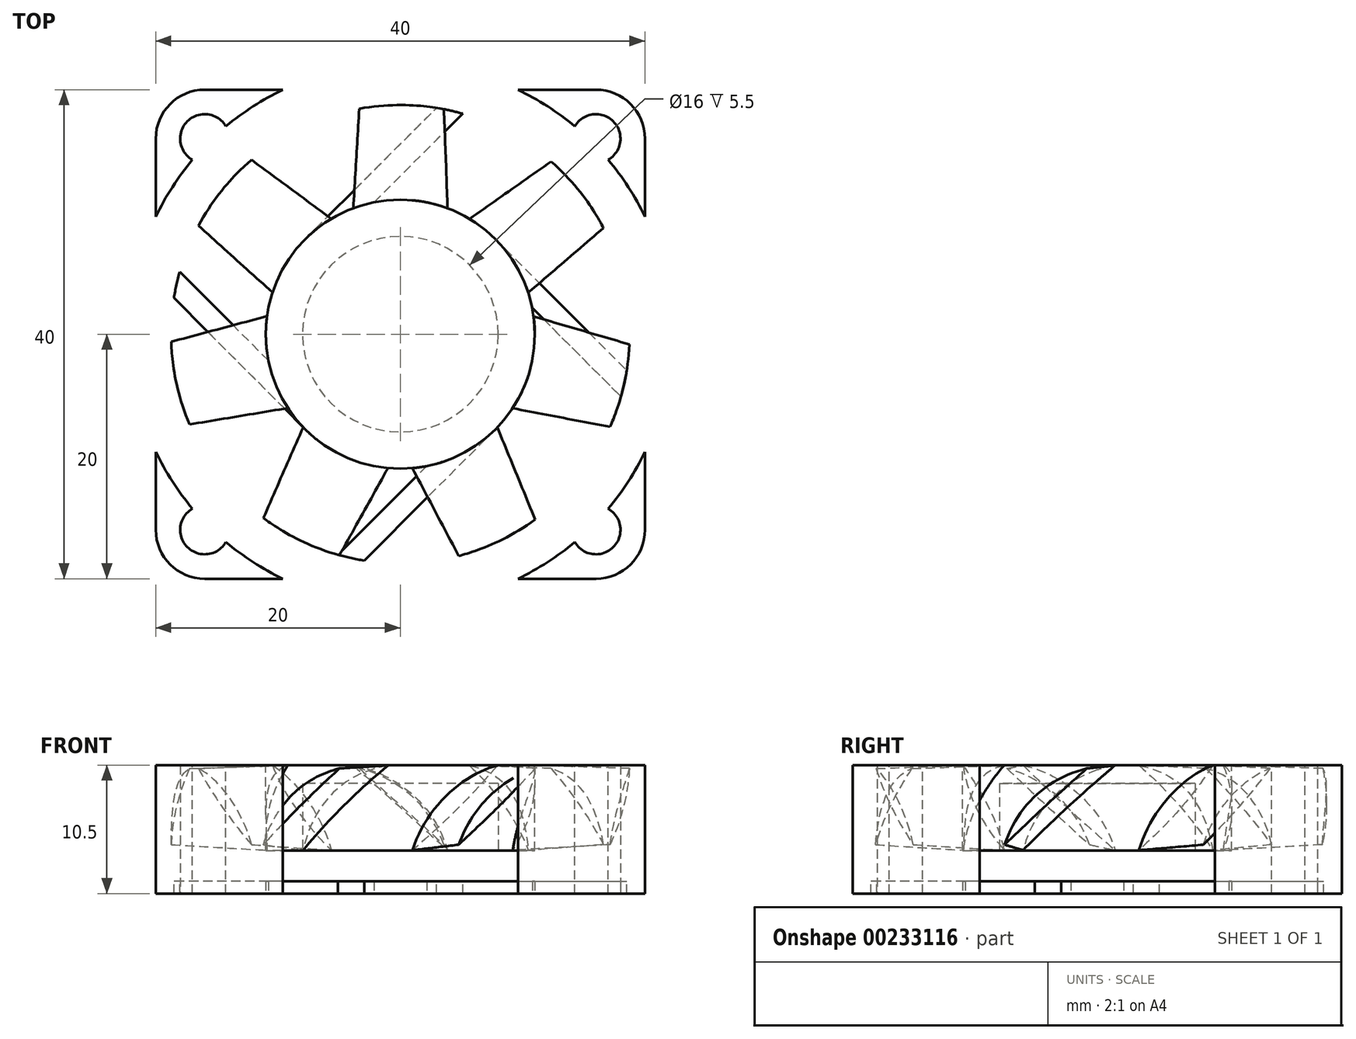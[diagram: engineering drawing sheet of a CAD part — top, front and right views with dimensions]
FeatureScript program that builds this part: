
annotation { "Feature Type Name" : "Feature", "Feature Type Description" : "" }
export const myFeature = defineFeature(function(context is Context, id is Id, definition is map)
    precondition{}
    {
        {
            var Q0;
            Q0=qCreatedBy(makeId("Top.planeOp"),FACE);
            var sketch = newSketch(context, id + "F0", { "sketchPlane" : qUnion([Q0])});
            skLineSegment(sketch, "E0.bottom", {"start": v(16, 20) * mm, "end": v(-16, 20) * mm});
            skLineSegment(sketch, "E0.top", {"start": v(16, -20) * mm, "end": v(-16, -20) * mm});
            skLineSegment(sketch, "E0.left", {"start": v(20, 16) * mm, "end": v(20, -16) * mm});
            skLineSegment(sketch, "E0.right", {"start": v(-20, 16) * mm, "end": v(-20, -16) * mm});
            skPoint(sketch, "E0.middle", {"position": v(0, 0) * mm});
            skPoint(sketch, "E1.visualSharp", {"position": v(20, 20) * mm});
            skArc(sketch, "E1.filletArc", {"start": v(20, 16) * mm, "mid": v(18.83, 18.83) * mm, "end": v(16, 20) * mm});
            skPoint(sketch, "E2.visualSharp", {"position": v(-20, 20) * mm});
            skArc(sketch, "E2.filletArc", {"start": v(-16, 20) * mm, "mid": v(-18.83, 18.83) * mm, "end": v(-20, 16) * mm});
            skPoint(sketch, "E3.visualSharp", {"position": v(-20, -20) * mm});
            skArc(sketch, "E3.filletArc", {"start": v(-20, -16) * mm, "mid": v(-18.83, -18.83) * mm, "end": v(-16, -20) * mm});
            skPoint(sketch, "E4.visualSharp", {"position": v(20, -20) * mm});
            skArc(sketch, "E4.filletArc", {"start": v(16, -20) * mm, "mid": v(18.83, -18.83) * mm, "end": v(20, -16) * mm});
            skLineSegment(sketch, "E5.bottom", {"start": v(-16, 16) * mm, "end": v(16, 16) * mm, "construction": true});
            skLineSegment(sketch, "E5.top", {"start": v(-16, -16) * mm, "end": v(16, -16) * mm, "construction": true});
            skLineSegment(sketch, "E5.left", {"start": v(-16, 16) * mm, "end": v(-16, -16) * mm, "construction": true});
            skLineSegment(sketch, "E5.right", {"start": v(16, 16) * mm, "end": v(16, -16) * mm, "construction": true});
            skCircle(sketch, "E6", {"center": v(-16, 16) * mm, "radius": 2 * mm});
            skCircle(sketch, "E7", {"center": v(16, 16) * mm, "radius": 2 * mm});
            skCircle(sketch, "E8", {"center": v(16, -16) * mm, "radius": 2 * mm});
            skCircle(sketch, "E9", {"center": v(-16, -16) * mm, "radius": 2 * mm});
            skSolve(sketch);
        }
        {
            var Q0;
            Q0=makeQuery(id+"F0.imprint","IMPRINT",FACE,{"disambiguationData":[TD([[makeQuery(id+"F0.imprint","IMPRINT",EDGE,{"derivedFrom":sQuery(id+"F0.wireOp",EDGE,"E0.bottom")}),1.0]])]});
            extrude(context, id + "F1", {"entities" : qUnion([Q0]), "depth" : 10.5 * mm});
        }
        {
            var Q0;
            Q0=qCreatedBy(makeId("Top.planeOp"),FACE);
            var sketch = newSketch(context, id + "F2", { "sketchPlane" : qUnion([Q0])});
            skCircle(sketch, "E10", {"center": v(0, 0) * mm, "radius": 19.25 * mm});
            skSolve(sketch);
        }
        {
            var Q0;
            Q0 = qSketchRegion(id + "F2", true);
            extrude(context, id + "F3", {"entities" : qUnion([Q0]), "operationType" : NewBodyOperationType.REMOVE, "endBound" : BoundingType.THROUGH_ALL, "depth" : 25 * mm});
        }
        {
            var Q0;
            Q0=qCreatedBy(makeId("Top.planeOp"),FACE);
            var sketch = newSketch(context, id + "F4", { "sketchPlane" : qUnion([Q0])});
            skArc(sketch, "E11", {"start": v(-7.78, -7.78) * mm, "mid": v(-3.19, -10.53) * mm, "end": v(2.15, -10.79) * mm});
            skLineSegment(sketch, "E12", {"start": v(-7.78, -7.78) * mm, "end": v(-20, 4.44) * mm});
            skLineSegment(sketch, "E13.0", {"start": v(-10.79, -2.15) * mm, "end": v(-20, 7.06) * mm});
            skLineSegment(sketch, "E14.1.0", {"start": v(2.15, -10.79) * mm, "end": v(-7.06, -20) * mm});
            skLineSegment(sketch, "E14.1.1", {"start": v(7.78, -7.78) * mm, "end": v(-4.44, -20) * mm});
            skLineSegment(sketch, "E14.2.0", {"start": v(10.79, 2.15) * mm, "end": v(20, -7.06) * mm});
            skLineSegment(sketch, "E14.2.1", {"start": v(7.78, 7.78) * mm, "end": v(20, -4.44) * mm});
            skLineSegment(sketch, "E14.3.0", {"start": v(-2.15, 10.79) * mm, "end": v(7.06, 20) * mm});
            skLineSegment(sketch, "E14.3.1", {"start": v(-7.78, 7.78) * mm, "end": v(4.44, 20) * mm});
            skArc(sketch, "E15.trimOffspring", {"start": v(-7.78, 7.78) * mm, "mid": v(-10.53, 3.19) * mm, "end": v(-10.79, -2.15) * mm});
            skArc(sketch, "E16.trimOffspring", {"start": v(7.78, 7.78) * mm, "mid": v(3.19, 10.53) * mm, "end": v(-2.15, 10.79) * mm});
            skArc(sketch, "E17.trimOffspring", {"start": v(7.78, -7.78) * mm, "mid": v(10.53, -3.19) * mm, "end": v(10.79, 2.15) * mm});
            skLineSegment(sketch, "E18", {"start": v(7.06, 20) * mm, "end": v(4.44, 20) * mm});
            skLineSegment(sketch, "E19", {"start": v(-20, 7.06) * mm, "end": v(-20, 4.44) * mm});
            skLineSegment(sketch, "E20", {"start": v(-7.06, -20) * mm, "end": v(-4.44, -20) * mm});
            skLineSegment(sketch, "E21", {"start": v(20, -7.06) * mm, "end": v(20, -4.44) * mm});
            skSolve(sketch);
        }
        {
            var Q0;
            Q0 = qSketchRegion(id + "F4", true);
            extrude(context, id + "F5", {"entities" : qUnion([Q0]), "operationType" : NewBodyOperationType.ADD, "depth" : 1 * mm});
        }
        {
            var Q0;
            Q0=makeQuery(id+"F1.opExtrude","CAP_FACE",FACE,{"disambiguationData":[OSD([sQuery(id+"F0.wireOp",EDGE,"E0.bottom"),sQuery(id+"F0.wireOp",EDGE,"E0.top"),sQuery(id+"F0.wireOp",EDGE,"E0.left"),sQuery(id+"F0.wireOp",EDGE,"E0.right"),sQuery(id+"F0.wireOp",EDGE,"E1.filletArc"),sQuery(id+"F0.wireOp",EDGE,"E2.filletArc"),sQuery(id+"F0.wireOp",EDGE,"E3.filletArc"),sQuery(id+"F0.wireOp",EDGE,"E4.filletArc"),sQuery(id+"F0.wireOp",EDGE,"E6"),sQuery(id+"F0.wireOp",EDGE,"E7"),sQuery(id+"F0.wireOp",EDGE,"E8"),sQuery(id+"F0.wireOp",EDGE,"E9")])],"isStart":false});
            var sketch = newSketch(context, id + "F6", { "sketchPlane" : qUnion([Q0])});
            skCircle(sketch, "E22", {"center": v(0, 0) * mm, "radius": 11 * mm});
            skSolve(sketch);
        }
        {
            var Q0;
            Q0 = qSketchRegion(id + "F6", true);
            extrude(context, id + "F7", {"entities" : qUnion([Q0]), "oppositeDirection" : true, "depth" : 7 * mm});
        }
        {
            var Q0;
            Q0=qCreatedBy(makeId("Front.planeOp"),FACE);
            cPlane(context, id + "F8", {"entities" : qUnion([Q0]), "cplaneType" : CPlaneType.OFFSET, "offset" : 9.5 * mm, "oppositeDirection" : true, "width" : 150 * mm, "height" : 150 * mm});
        }
        {
            var Q0;
            Q0=qCreatedBy(id+"F8.planeOp",FACE);
            var sketch = newSketch(context, id + "F9", { "sketchPlane" : qUnion([Q0])});
            skLineSegment(sketch, "E23", {"start": v(0, 0) * mm, "end": v(0, 7) * mm, "construction": true});
            skPoint(sketch, "E24", {"position": v(0, 3.5) * mm});
            skLineSegment(sketch, "E25", {"start": v(3.89, 3.5) * mm, "end": v(-3.89, 10.5) * mm});
            skArc(sketch, "E26", {"start": v(3.89, 3.5) * mm, "mid": v(1, 8.11) * mm, "end": v(-3.89, 10.5) * mm});
            skSolve(sketch);
        }
        {
            var Q0;
            Q0 = qSketchRegion(id + "F9", true);
            extrude(context, id + "F10", {"entities" : qUnion([Q0]), "oppositeDirection" : true, "depth" : 10 * mm, "hasDraft" : true, "draftAngle" : 1 * degree, "draftPullDirection" : true});
        }
        {
            var Q0;
            Q0=makeQuery(id+"F10.opExtrude","SWEPT_BODY",BODY,{"disambiguationData":[OSD([sQuery(id+"F9.wireOp",EDGE,"E25"),sQuery(id+"F9.wireOp",EDGE,"E26")])]});
            var Q1;
            Q1=makeQuery(id+"F7.opExtrude","SWEPT_FACE",FACE,{"disambiguationData":[OSD([sQuery(id+"F6.wireOp",EDGE,"E22")])]});
            circularPattern(context, id + "F11", {"operationType" : NewBodyOperationType.ADD, "entities" : qUnion([Q0]), "axis" : qUnion([Q1]), "angle" : 360 * degree, "instanceCount" : 7, "equalSpace" : true});
        }
        {
            var Q0;
            Q0=makeQuery(id+"F7.opExtrude","CAP_FACE",FACE,{"disambiguationData":[OSD([sQuery(id+"F6.wireOp",EDGE,"E22")])],"isStart":true});
            var sketch = newSketch(context, id + "F12", { "sketchPlane" : qUnion([Q0])});
            skCircle(sketch, "E27", {"center": v(0, 0) * mm, "radius": 18.75 * mm});
            skCircle(sketch, "E28", {"center": v(0, 0) * mm, "radius": 22.2 * mm});
            skSolve(sketch);
        }
        {
            var Q0;
            Q0 = qSketchRegion(id + "F12", true);
            extrude(context, id + "F13", {"entities" : qUnion([Q0]), "operationType" : NewBodyOperationType.REMOVE, "endBound" : BoundingType.THROUGH_ALL, "oppositeDirection" : true, "depth" : 25 * mm});
        }
        {
            var Q0;
            Q0=makeQuery(id+"F5.opExtrude","CAP_FACE",FACE,{"disambiguationData":[OSD([sQuery(id+"F4.wireOp",EDGE,"E11"),sQuery(id+"F4.wireOp",EDGE,"E12"),sQuery(id+"F4.wireOp",EDGE,"E13.0"),sQuery(id+"F4.wireOp",EDGE,"E14.1.0"),sQuery(id+"F4.wireOp",EDGE,"E14.1.1"),sQuery(id+"F4.wireOp",EDGE,"E14.2.0"),sQuery(id+"F4.wireOp",EDGE,"E14.2.1"),sQuery(id+"F4.wireOp",EDGE,"E14.3.0"),sQuery(id+"F4.wireOp",EDGE,"E14.3.1"),sQuery(id+"F4.wireOp",EDGE,"E15.trimOffspring"),sQuery(id+"F4.wireOp",EDGE,"E16.trimOffspring"),sQuery(id+"F4.wireOp",EDGE,"E17.trimOffspring"),sQuery(id+"F4.wireOp",EDGE,"E18"),sQuery(id+"F4.wireOp",EDGE,"E19"),sQuery(id+"F4.wireOp",EDGE,"E20"),sQuery(id+"F4.wireOp",EDGE,"E21")])],"isStart":false});
            var sketch = newSketch(context, id + "F14", { "sketchPlane" : qUnion([Q0])});
            skCircle(sketch, "E29", {"center": v(0, 0) * mm, "radius": 8 * mm});
            skSolve(sketch);
        }
        {
            var Q0;
            Q0 = qSketchRegion(id + "F14", true);
            extrude(context, id + "F15", {"entities" : qUnion([Q0]), "operationType" : NewBodyOperationType.ADD, "depth" : 8 * mm});
        }
        {
            var Q0;
            Q0 = qSketchRegion(id + "F14", true);
            extrude(context, id + "F16", {"entities" : qUnion([Q0]), "operationType" : NewBodyOperationType.REMOVE, "depth" : 8 * mm});
        }
    });
